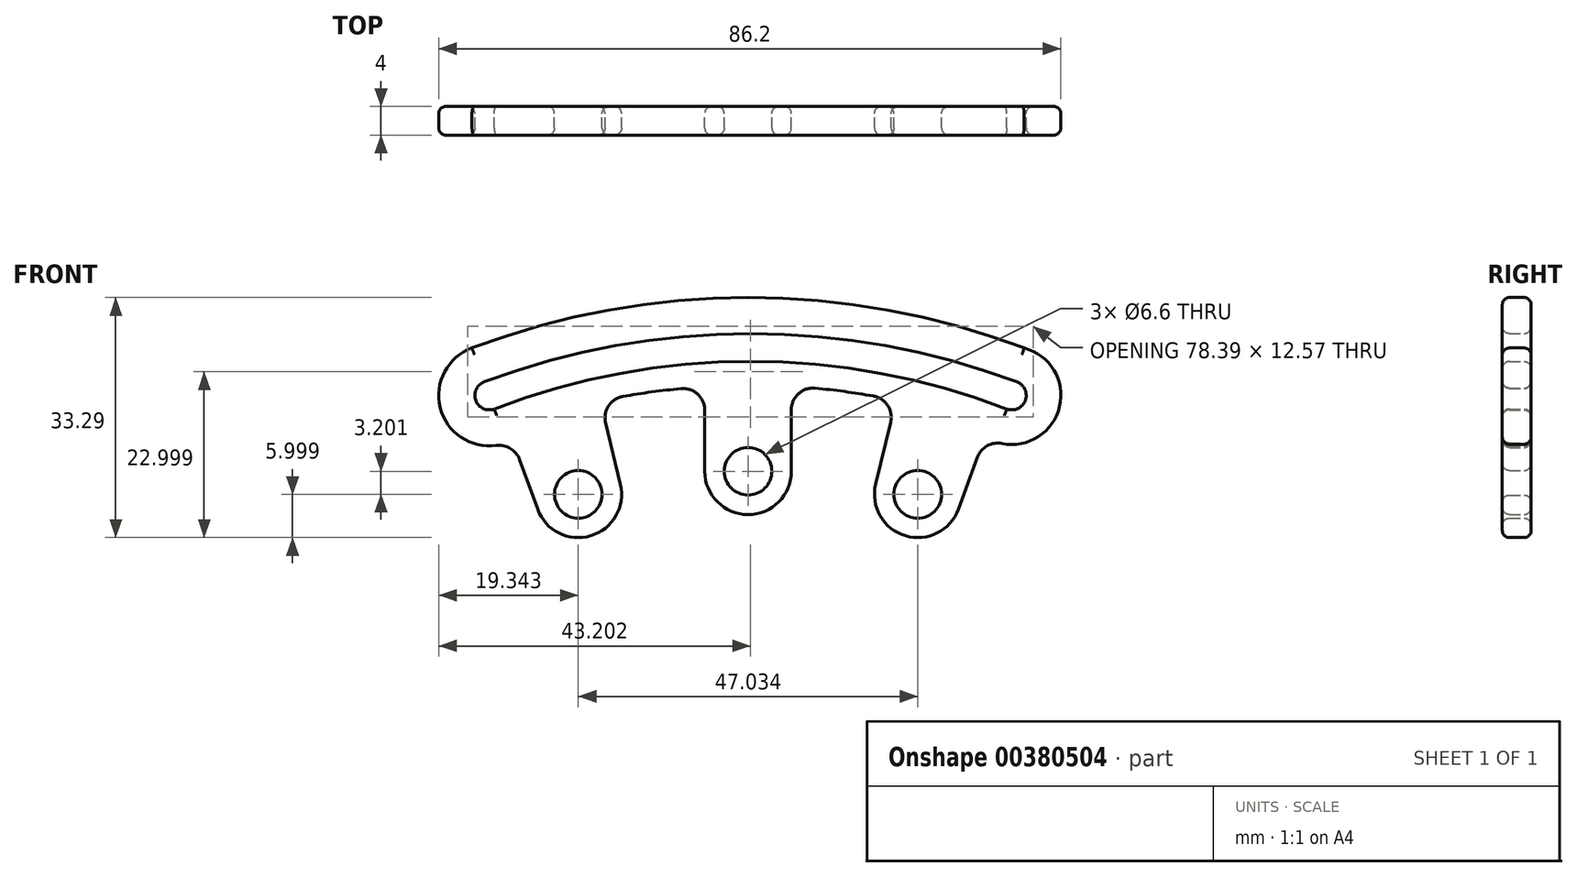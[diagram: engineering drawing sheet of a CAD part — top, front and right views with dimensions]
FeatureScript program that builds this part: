
annotation { "Feature Type Name" : "Feature", "Feature Type Description" : "" }
export const myFeature = defineFeature(function(context is Context, id is Id, definition is map)
    precondition{}
    {
        {
            var Q0;
            Q0=qCreatedBy(makeId("Front.planeOp"),FACE);
            var sketch = newSketch(context, id + "F0", { "sketchPlane" : qUnion([Q0])});
            skLineSegment(sketch, "E0", {"start": v(0, 0) * mm, "end": v(0, 189.24) * mm, "construction": true});
            skCircle(sketch, "E1", {"center": v(0, 88) * mm, "radius": 3.3 * mm});
            skCircle(sketch, "E2", {"center": v(23.52, 84.8) * mm, "radius": 3.3 * mm});
            skCircle(sketch, "E3", {"center": v(-23.52, 84.8) * mm, "radius": 3.3 * mm});
            skLineSegment(sketch, "E4", {"start": v(0, 0) * mm, "end": v(23.52, 84.8) * mm, "construction": true});
            skLineSegment(sketch, "E5", {"start": v(0, 0) * mm, "end": v(-23.52, 84.8) * mm, "construction": true});
            skArc(sketch, "E6", {"start": v(23.52, 84.8) * mm, "mid": v(0, 88) * mm, "end": v(-23.52, 84.8) * mm, "construction": true});
            skCircle(sketch, "E7", {"center": v(-23.52, 84.8) * mm, "radius": 6 * mm, "construction": true});
            skCircle(sketch, "E8", {"center": v(0, 88) * mm, "radius": 6 * mm, "construction": true});
            skCircle(sketch, "E9", {"center": v(23.52, 84.8) * mm, "radius": 6 * mm, "construction": true});
            skLineSegment(sketch, "E10", {"start": v(-23.52, 84.8) * mm, "end": v(23.52, 84.8) * mm, "construction": true});
            skLineSegment(sketch, "E11", {"start": v(-23.52, 84.8) * mm, "end": v(-17.68, 86.2) * mm, "construction": true});
            skLineSegment(sketch, "E12", {"start": v(0, 88) * mm, "end": v(69.3, 88) * mm, "construction": true});
            skLineSegment(sketch, "E13", {"start": v(69.3, 88) * mm, "end": v(69.3, 0) * mm, "construction": true});
            skLineSegment(sketch, "E14", {"start": v(0, 88) * mm, "end": v(6, 88) * mm, "construction": true});
            skLineSegment(sketch, "E15", {"start": v(6, 88) * mm, "end": v(6, 96.53) * mm});
            skLineSegment(sketch, "E16", {"start": v(0, 88) * mm, "end": v(-6, 88) * mm, "construction": true});
            skLineSegment(sketch, "E17", {"start": v(-6, 88) * mm, "end": v(-6, 96.47) * mm});
            skLineSegment(sketch, "E18", {"start": v(-23.52, 84.8) * mm, "end": v(-17.52, 84.8) * mm});
            skLineSegment(sketch, "E19", {"start": v(-17.68, 86.2) * mm, "end": v(-19.73, 94.72) * mm});
            skLineSegment(sketch, "E20", {"start": v(23.52, 84.8) * mm, "end": v(17.68, 86.2) * mm});
            skLineSegment(sketch, "E21", {"start": v(17.68, 86.2) * mm, "end": v(19.75, 94.78) * mm});
            skLineSegment(sketch, "E22", {"start": v(-35.17, 96.63) * mm, "end": v(35.86, 96.63) * mm, "construction": true});
            skArc(sketch, "E23", {"start": v(35.86, 96.63) * mm, "mid": v(0.34, 103.22) * mm, "end": v(-35.17, 96.63) * mm});
            skArc(sketch, "E24", {"start": v(-36.54, 100.4) * mm, "mid": v(-37.74, 97.83) * mm, "end": v(-35.17, 96.63) * mm});
            skArc(sketch, "E25", {"start": v(35.86, 96.63) * mm, "mid": v(38.42, 97.83) * mm, "end": v(37.22, 100.4) * mm});
            skArc(sketch, "E26", {"start": v(37.22, 100.4) * mm, "mid": v(0.34, 107.08) * mm, "end": v(-36.54, 100.4) * mm});
            skCircle(sketch, "E27", {"center": v(-35.86, 98.51) * mm, "radius": 3 * mm, "construction": true});
            skCircle(sketch, "E28", {"center": v(36.54, 98.51) * mm, "radius": 3 * mm, "construction": true});
            skLineSegment(sketch, "E29", {"start": v(-36.88, 101.33) * mm, "end": v(37.57, 101.33) * mm, "construction": true});
            skLineSegment(sketch, "E30", {"start": v(37.57, 101.33) * mm, "end": v(35.51, 95.7) * mm, "construction": true});
            skLineSegment(sketch, "E31", {"start": v(35.51, 95.7) * mm, "end": v(-34.83, 95.7) * mm, "construction": true});
            skArc(sketch, "E32", {"start": v(36.54, 98.51) * mm, "mid": v(0.34, 105.05) * mm, "end": v(-35.86, 98.51) * mm, "construction": true});
            skLineSegment(sketch, "E33", {"start": v(-38.25, 105.1) * mm, "end": v(38.25, 105.1) * mm, "construction": true});
            skLineSegment(sketch, "E34", {"start": v(-34.15, 93.81) * mm, "end": v(-34.15, 93.81) * mm, "construction": true});
            skArc(sketch, "E35", {"start": v(38.25, 105.1) * mm, "mid": v(0, 112.1) * mm, "end": v(-38.25, 105.1) * mm});
            skLineSegment(sketch, "E36", {"start": v(-23.52, 84.8) * mm, "end": v(-29.16, 82.75) * mm, "construction": true});
            skArc(sketch, "E37", {"start": v(-38.25, 105.1) * mm, "mid": v(-42.65, 96.83) * mm, "end": v(-34.9, 91.58) * mm});
            skArc(sketch, "E38", {"start": v(-9.28, 99.46) * mm, "mid": v(-13.32, 99) * mm, "end": v(-17.34, 98.37) * mm});
            skArc(sketch, "E39", {"start": v(17.35, 98.43) * mm, "mid": v(13.33, 99.06) * mm, "end": v(9.28, 99.52) * mm});
            skPoint(sketch, "E40.visualSharp", {"position": v(-20.47, 97.77) * mm});
            skArc(sketch, "E40.filletArc", {"start": v(-17.34, 98.37) * mm, "mid": v(-19.33, 97.06) * mm, "end": v(-19.73, 94.72) * mm});
            skPoint(sketch, "E41.visualSharp", {"position": v(-6, 99.7) * mm});
            skArc(sketch, "E41.filletArc", {"start": v(-6, 96.47) * mm, "mid": v(-6.98, 98.69) * mm, "end": v(-9.28, 99.46) * mm});
            skPoint(sketch, "E42.visualSharp", {"position": v(6, 99.77) * mm});
            skArc(sketch, "E42.filletArc", {"start": v(9.28, 99.52) * mm, "mid": v(6.98, 98.75) * mm, "end": v(6, 96.53) * mm});
            skPoint(sketch, "E43.visualSharp", {"position": v(20.48, 97.83) * mm});
            skArc(sketch, "E43.filletArc", {"start": v(19.75, 94.78) * mm, "mid": v(19.34, 97.12) * mm, "end": v(17.35, 98.43) * mm});
            skArc(sketch, "E44", {"start": v(-29.16, 82.75) * mm, "mid": v(-21.79, 79.05) * mm, "end": v(-17.68, 86.2) * mm});
            skArc(sketch, "E45", {"start": v(-6, 88) * mm, "mid": v(0, 82) * mm, "end": v(6, 88) * mm});
            skLineSegment(sketch, "E46", {"start": v(23.52, 84.8) * mm, "end": v(29.16, 82.75) * mm, "construction": true});
            skLineSegment(sketch, "E47", {"start": v(29.16, 82.75) * mm, "end": v(31.77, 89.94) * mm});
            skArc(sketch, "E48", {"start": v(35.19, 91.85) * mm, "mid": v(43.16, 96.98) * mm, "end": v(38.25, 105.1) * mm});
            skArc(sketch, "E49.filletArc", {"start": v(35.19, 91.85) * mm, "mid": v(33.12, 91.53) * mm, "end": v(31.77, 89.94) * mm});
            skLineSegment(sketch, "E50", {"start": v(-29.16, 82.75) * mm, "end": v(-31.66, 89.63) * mm});
            skArc(sketch, "E51.filletArc", {"start": v(-31.66, 89.63) * mm, "mid": v(-32.93, 91.18) * mm, "end": v(-34.9, 91.58) * mm});
            skArc(sketch, "E52", {"start": v(17.68, 86.2) * mm, "mid": v(21.79, 79.05) * mm, "end": v(29.16, 82.75) * mm});
            skSolve(sketch);
        }
        {
            var Q0;
            Q0=qSketchRegion(id+"F0",true);
            extrude(context, id + "F1", {"entities" : qUnion([Q0]), "depth" : 4 * mm});
        }
        {
            var Q0;
            Q0=makeQuery(id+"F1.opExtrude","CAP_EDGE",EDGE,{"disambiguationData":[OSD([sQuery(id+"F0.wireOp",EDGE,"E35")])],"isStart":false});
            var Q1;
            Q1=makeQuery(id+"F1.opExtrude","CAP_FACE",FACE,{"disambiguationData":[OSD([sQuery(id+"F0.wireOp",EDGE,"E1"),sQuery(id+"F0.wireOp",EDGE,"E2"),sQuery(id+"F0.wireOp",EDGE,"E3"),sQuery(id+"F0.wireOp",EDGE,"E15"),sQuery(id+"F0.wireOp",EDGE,"E17"),sQuery(id+"F0.wireOp",EDGE,"E19"),sQuery(id+"F0.wireOp",EDGE,"E21"),sQuery(id+"F0.wireOp",EDGE,"E23"),sQuery(id+"F0.wireOp",EDGE,"E24"),sQuery(id+"F0.wireOp",EDGE,"E25"),sQuery(id+"F0.wireOp",EDGE,"E26"),sQuery(id+"F0.wireOp",EDGE,"E35"),sQuery(id+"F0.wireOp",EDGE,"E37"),sQuery(id+"F0.wireOp",EDGE,"E38"),sQuery(id+"F0.wireOp",EDGE,"E39"),sQuery(id+"F0.wireOp",EDGE,"E40.filletArc"),sQuery(id+"F0.wireOp",EDGE,"E41.filletArc"),sQuery(id+"F0.wireOp",EDGE,"E42.filletArc"),sQuery(id+"F0.wireOp",EDGE,"E43.filletArc"),sQuery(id+"F0.wireOp",EDGE,"E44"),sQuery(id+"F0.wireOp",EDGE,"E45"),sQuery(id+"F0.wireOp",EDGE,"E47"),sQuery(id+"F0.wireOp",EDGE,"E48"),sQuery(id+"F0.wireOp",EDGE,"E49.filletArc"),sQuery(id+"F0.wireOp",EDGE,"E50"),sQuery(id+"F0.wireOp",EDGE,"E51.filletArc"),sQuery(id+"F0.wireOp",EDGE,"E52")])],"isStart":false});
            var Q2;
            Q2=makeQuery(id+"F1.opExtrude","CAP_FACE",FACE,{"disambiguationData":[OSD([sQuery(id+"F0.wireOp",EDGE,"E1"),sQuery(id+"F0.wireOp",EDGE,"E2"),sQuery(id+"F0.wireOp",EDGE,"E3"),sQuery(id+"F0.wireOp",EDGE,"E15"),sQuery(id+"F0.wireOp",EDGE,"E17"),sQuery(id+"F0.wireOp",EDGE,"E19"),sQuery(id+"F0.wireOp",EDGE,"E21"),sQuery(id+"F0.wireOp",EDGE,"E23"),sQuery(id+"F0.wireOp",EDGE,"E24"),sQuery(id+"F0.wireOp",EDGE,"E25"),sQuery(id+"F0.wireOp",EDGE,"E26"),sQuery(id+"F0.wireOp",EDGE,"E35"),sQuery(id+"F0.wireOp",EDGE,"E37"),sQuery(id+"F0.wireOp",EDGE,"E38"),sQuery(id+"F0.wireOp",EDGE,"E39"),sQuery(id+"F0.wireOp",EDGE,"E40.filletArc"),sQuery(id+"F0.wireOp",EDGE,"E41.filletArc"),sQuery(id+"F0.wireOp",EDGE,"E42.filletArc"),sQuery(id+"F0.wireOp",EDGE,"E43.filletArc"),sQuery(id+"F0.wireOp",EDGE,"E44"),sQuery(id+"F0.wireOp",EDGE,"E45"),sQuery(id+"F0.wireOp",EDGE,"E47"),sQuery(id+"F0.wireOp",EDGE,"E48"),sQuery(id+"F0.wireOp",EDGE,"E49.filletArc"),sQuery(id+"F0.wireOp",EDGE,"E50"),sQuery(id+"F0.wireOp",EDGE,"E51.filletArc"),sQuery(id+"F0.wireOp",EDGE,"E52")])],"isStart":true});
            fillet(context, id + "F2", {"entities" : qUnion([Q0, Q1, Q2]), "radius" : 1 * mm, "tangentPropagation" : true, "allowEdgeOverflow" : false});
        }
    });
